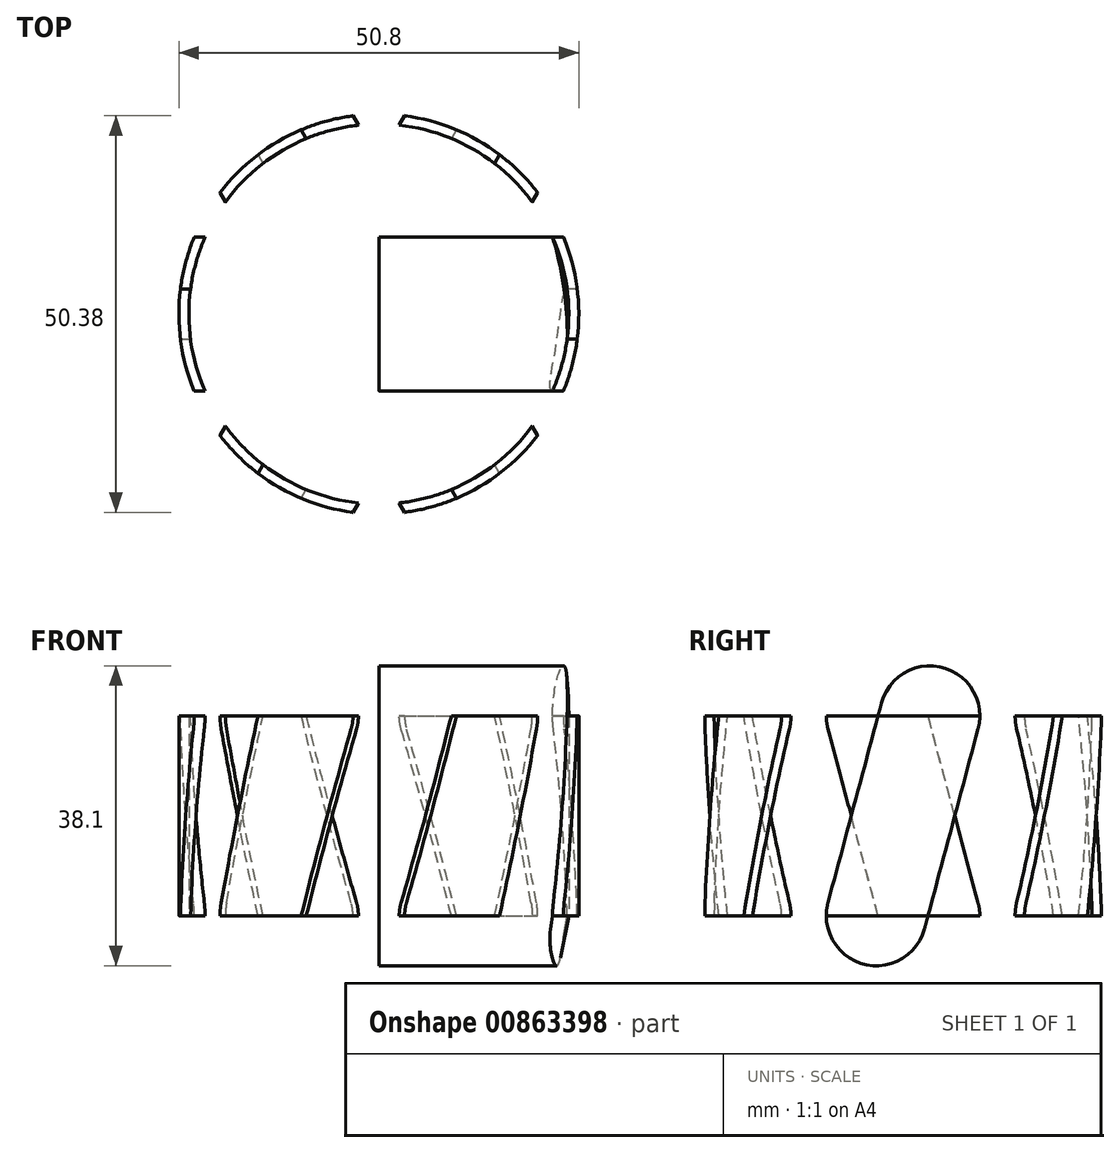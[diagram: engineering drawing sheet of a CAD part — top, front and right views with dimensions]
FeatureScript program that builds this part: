
annotation { "Feature Type Name" : "Feature", "Feature Type Description" : "" }
export const myFeature = defineFeature(function(context is Context, id is Id, definition is map)
    precondition{}
    {
        {
            var Q0;
            Q0=qCreatedBy(makeId("Right.planeOp"),FACE);
            var sketch = newSketch(context, id + "F0", { "sketchPlane" : qUnion([Q0])});
            skLineSegment(sketch, "E0", {"start": v(-16.8, 0) * mm, "end": v(-19.05, 0) * mm});
            skLineSegment(sketch, "E1", {"start": v(0, 6.35) * mm, "end": v(0, 25.4) * mm});
            skLineSegment(sketch, "E2", {"start": v(0, 25.4) * mm, "end": v(-24.13, 25.4) * mm});
            skLineSegment(sketch, "E3", {"start": v(-24.13, 25.4) * mm, "end": v(-19.05, 0) * mm});
            skLineSegment(sketch, "E4", {"start": v(-24.13, 25.4) * mm, "end": v(-24.13, 50.8) * mm});
            skLineSegment(sketch, "E5", {"start": v(0, 25.4) * mm, "end": v(0, 50.8) * mm});
            skLineSegment(sketch, "E6", {"start": v(0, 50.8) * mm, "end": v(25.4, 50.8) * mm});
            skArc(sketch, "E7", {"start": v(-3.06, 91.33) * mm, "mid": v(-18.55, 73.64) * mm, "end": v(-24.13, 50.8) * mm});
            skLineSegment(sketch, "E8", {"start": v(0, 50.8) * mm, "end": v(0, 93.32) * mm});
            skArc(sketch, "E9", {"start": v(0, 92.3) * mm, "mid": v(-1.6, 92.05) * mm, "end": v(-3.06, 91.33) * mm});
            skLineSegment(sketch, "E10", {"start": v(0, 0) * mm, "end": v(0, -19.05) * mm});
            skArc(sketch, "E11", {"start": v(0, 6.35) * mm, "mid": v(-8.98, 4.7) * mm, "end": v(-16.8, 0) * mm});
            skSolve(sketch);
        }
        {
            var Q0;
            Q0=makeQuery(id+"F0.imprint","IMPRINT",FACE,{"disambiguationData":[TD([[makeQuery(id+"F0.imprint","IMPRINT",EDGE,{"derivedFrom":sQuery(id+"F0.wireOp",EDGE,"E0")}),-1.0]])]});
            var Q1;
            Q1=makeQuery(id+"F0.imprint","IMPRINT",FACE,{"disambiguationData":[TD([[makeQuery(id+"F0.imprint","IMPRINT",EDGE,{"derivedFrom":sQuery(id+"F0.wireOp",EDGE,"E2")}),-1.0]])]});
            var Q2;
            Q2=sQuery(id+"F0.wireOp",EDGE,"E8");
            revolve(context, id + "F1", {"surfaceOperationType" : NewSurfaceOperationType.NEW, "entities" : qUnion([Q0, Q1]), "axis" : qUnion([Q2]), "revolveType" : RevolveType.FULL});
        }
        {
            var Q0;
            Q0=qCreatedBy(makeId("Right.planeOp"),FACE);
            var sketch = newSketch(context, id + "F2", { "sketchPlane" : qUnion([Q0])});
            skLineSegment(sketch, "E12", {"start": v(0, 0) * mm, "end": v(0, 25.4) * mm});
            skLineSegment(sketch, "E13", {"start": v(0, 25.4) * mm, "end": v(-25.4, 25.4) * mm});
            skLineSegment(sketch, "E14", {"start": v(-25.4, 25.4) * mm, "end": v(-25.4, 50.8) * mm});
            skLineSegment(sketch, "E15", {"start": v(-25.4, 50.8) * mm, "end": v(-24.13, 50.8) * mm});
            skLineSegment(sketch, "E16", {"start": v(-24.13, 50.8) * mm, "end": v(-24.13, 25.4) * mm});
            skSolve(sketch);
        }
        {
            var Q0;
            {var subQ0=sQuery(id+"F2.wireOp",EDGE,"E14");Q0=makeQuery(id+"F2.imprint","IMPRINT",FACE,{"disambiguationData":[TD([[makeQuery(id+"F2.imprint","IMPRINT",EDGE,{"derivedFrom":subQ0}),-1.0]])]});}
            var Q1;
            Q1=sQuery(id+"F2.wireOp",EDGE,"E12");
            revolve(context, id + "F3", {"surfaceOperationType" : NewSurfaceOperationType.NEW, "entities" : qUnion([Q0]), "axis" : qUnion([Q1]), "revolveType" : RevolveType.FULL});
        }
        {
            var Q0;
            Q0=qCreatedBy(makeId("Right.planeOp"),FACE);
            var sketch = newSketch(context, id + "F4", { "sketchPlane" : qUnion([Q0])});
            skLineSegment(sketch, "E17", {"start": v(0, 38.1) * mm, "end": v(-3.4, 25.4) * mm});
            skLineSegment(sketch, "E18", {"start": v(-3.4, 25.4) * mm, "end": v(3.4, 50.8) * mm});
            skPoint(sketch, "E19.orphan", {"position": v(0, 52.8) * mm});
            skPoint(sketch, "E20.orphan", {"position": v(0, 23.4) * mm});
            skPoint(sketch, "E21.orphan", {"position": v(-25.4, 52.8) * mm});
            skArc(sketch, "E22.0.startCap", {"start": v(2.73, 23.76) * mm, "mid": v(-5.05, 19.27) * mm, "end": v(-9.54, 27.04) * mm});
            skArc(sketch, "E22.0.endCap", {"start": v(-2.73, 52.44) * mm, "mid": v(5.05, 56.93) * mm, "end": v(9.54, 49.16) * mm});
            skLineSegment(sketch, "E22.0.left", {"start": v(-9.54, 27.04) * mm, "end": v(-2.73, 52.44) * mm});
            skLineSegment(sketch, "E22.0.right", {"start": v(2.73, 23.76) * mm, "end": v(9.54, 49.16) * mm});
            skSolve(sketch);
        }
        {
            var Q0;
            Q0=qSketchRegion(id+"F4",true);
            extrude(context, id + "F5", {"entities" : qUnion([Q0]), "operationType" : NewBodyOperationType.INTERSECT, "depth" : 25.4 * mm, "offsetDistance" : 25.4 * mm});
        }
        {
            var Q0;
            Q0=makeQuery(id+"F3.opRevolve","SWEPT_BODY",BODY,{"disambiguationData":[OSD([sQuery(id+"F2.wireOp",EDGE,"E13"),sQuery(id+"F2.wireOp",EDGE,"E14"),sQuery(id+"F2.wireOp",EDGE,"E15"),sQuery(id+"F2.wireOp",EDGE,"E16")])]});
            var Q1;
            Q1=makeQuery(id+"F1.opRevolve","SWEPT_FACE",FACE,{"disambiguationData":[OSD([sQuery(id+"F0.wireOp",EDGE,"E4")])]});
            circularPattern(context, id + "F6", {"entities" : qUnion([Q0]), "axis" : qUnion([Q1]), "angle" : 360 * degree, "instanceCount" : 6, "equalSpace" : true});
        }
    });
